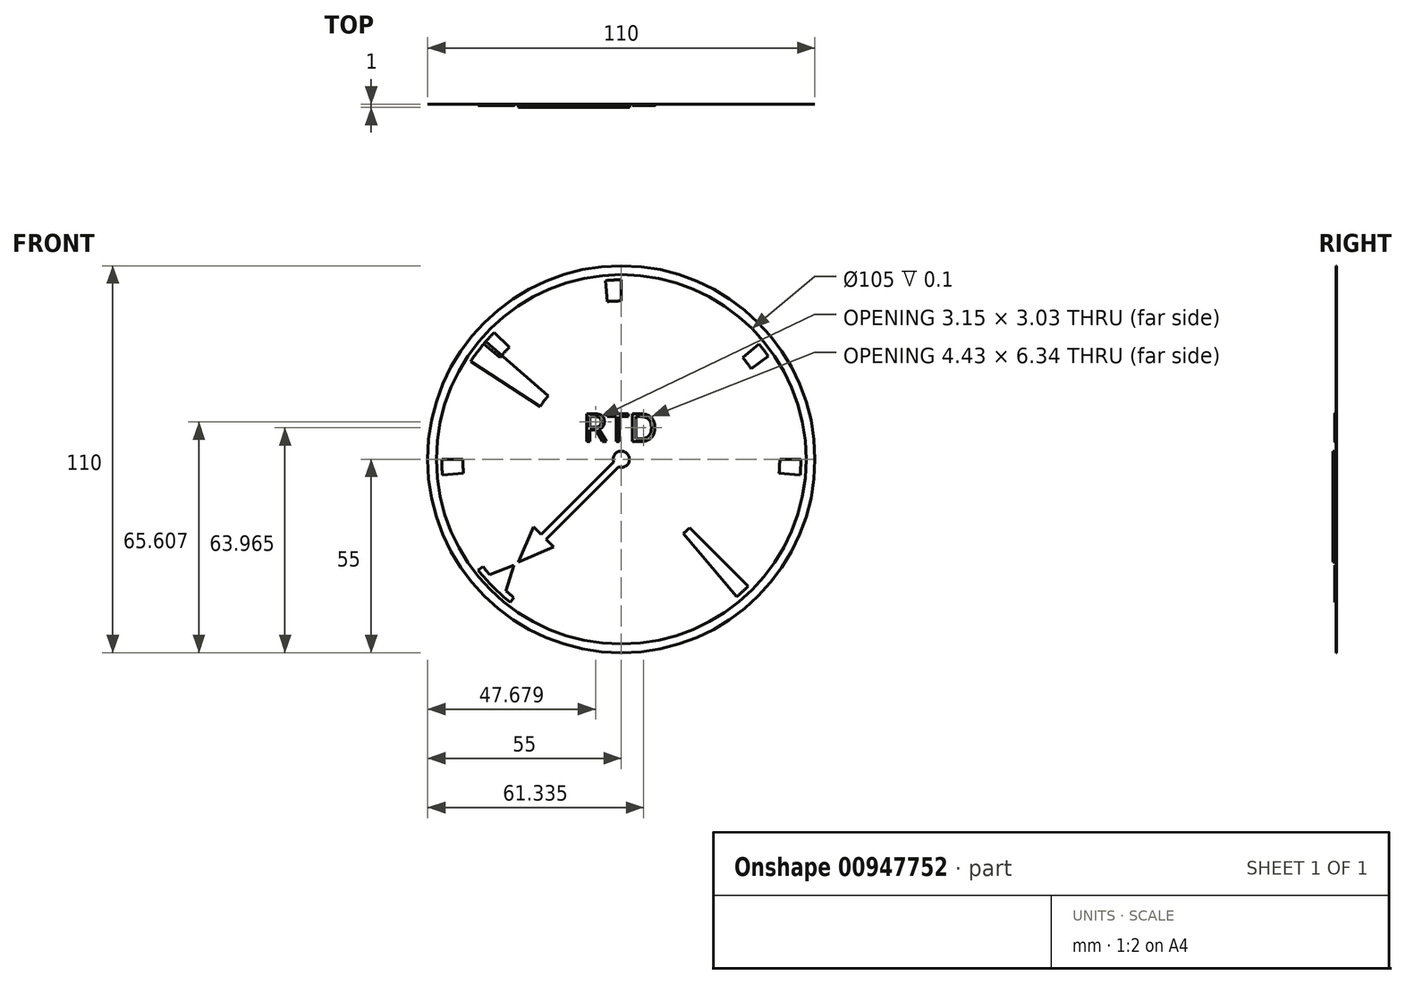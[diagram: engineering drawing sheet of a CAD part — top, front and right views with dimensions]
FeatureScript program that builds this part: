
annotation { "Feature Type Name" : "Feature", "Feature Type Description" : "" }
export const myFeature = defineFeature(function(context is Context, id is Id, definition is map)
    precondition{}
    {
        {
            var Q0;
            Q0=qCreatedBy(makeId("Right.planeOp"),FACE);
            var sketch = newSketch(context, id + "F0", { "sketchPlane" : qUnion([Q0])});
            skLineSegment(sketch, "E0", {"start": v(0, 0) * mm, "end": v(-116.06, 0) * mm, "construction": true});
            skSolve(sketch);
        }
        {
            var Q0;
            Q0=qCreatedBy(makeId("Right.planeOp"),FACE);
            var Q1;
            Q1=sQuery(id+"F0.wireOp",EDGE,"E0");
            cPlane(context, id + "F1", {"entities" : qUnion([Q0, Q1]), "cplaneType" : CPlaneType.LINE_ANGLE, "offset" : 25 * mm, "angle" : 135 * degree, "width" : 150 * mm, "height" : 150 * mm});
        }
        {
            var Q0;
            Q0=qCreatedBy(id+"F1.planeOp",FACE);
            var sketch = newSketch(context, id + "F2", { "sketchPlane" : qUnion([Q0])});
            skLineSegment(sketch, "E1.bottom", {"start": v(-25.4, 0) * mm, "end": v(-50.8, 0) * mm});
            skLineSegment(sketch, "E1.top", {"start": v(-25.4, 0) * mm, "end": v(-50.8, 0) * mm});
            skLineSegment(sketch, "E1.left", {"start": v(-25.4, 0) * mm, "end": v(-25.4, 0) * mm});
            skLineSegment(sketch, "E1.right", {"start": v(-50.8, 0) * mm, "end": v(-50.8, 0) * mm});
            skSolve(sketch);
        }
        {
            var Q0;
            Q0=qSketchRegion(id+"F2",true);
            var Q1;
            Q1=sQuery(id+"F0.wireOp",EDGE,"E0");
            revolve(context, id + "F3", {"surfaceOperationType" : NewSurfaceOperationType.NEW, "entities" : qUnion([Q0]), "axis" : qUnion([Q1]), "revolveType" : RevolveType.ONE_DIRECTION, "oppositeDirection" : true, "angle" : 135 * degree});
        }
        {
            var Q0;
            Q0=qCreatedBy(makeId("Right.planeOp"),FACE);
            var sketch = newSketch(context, id + "F4", { "sketchPlane" : qUnion([Q0])});
            skLineSegment(sketch, "E2.bottom", {"start": v(-0.01, 50.8) * mm, "end": v(0, 50.8) * mm});
            skLineSegment(sketch, "E2.top", {"start": v(0, 25.4) * mm, "end": v(0, 25.4) * mm});
            skLineSegment(sketch, "E2.left", {"start": v(-0.01, 50.8) * mm, "end": v(0, 25.4) * mm});
            skLineSegment(sketch, "E2.right", {"start": v(0, 50.8) * mm, "end": v(0, 25.4) * mm});
            skSolve(sketch);
        }
        {
            var Q0;
            Q0=qSketchRegion(id+"F4",true);
            var Q1;
            Q1=sQuery(id+"F0.wireOp",EDGE,"E0");
            revolve(context, id + "F5", {"surfaceOperationType" : NewSurfaceOperationType.NEW, "entities" : qUnion([Q0]), "axis" : qUnion([Q1]), "revolveType" : RevolveType.ONE_DIRECTION, "oppositeDirection" : true, "angle" : 2 * degree});
        }
        {
            var Q0;
            Q0=qCreatedBy(makeId("Right.planeOp"),FACE);
            var Q1;
            Q1=sQuery(id+"F0.wireOp",EDGE,"E0");
            cPlane(context, id + "F6", {"entities" : qUnion([Q0, Q1]), "cplaneType" : CPlaneType.LINE_ANGLE, "offset" : 25 * mm, "angle" : 2 * degree, "oppositeDirection" : true, "width" : 150 * mm, "height" : 150 * mm});
        }
        {
            var Q0;
            Q0=qCreatedBy(id+"F6.planeOp",FACE);
            var sketch = newSketch(context, id + "F7", { "sketchPlane" : qUnion([Q0])});
            skLineSegment(sketch, "E3.bottom", {"start": v(0, 50.8) * mm, "end": v(0, 50.8) * mm});
            skLineSegment(sketch, "E3.top", {"start": v(0, 25.4) * mm, "end": v(0, 25.4) * mm});
            skLineSegment(sketch, "E3.left", {"start": v(0, 50.8) * mm, "end": v(0, 25.4) * mm});
            skLineSegment(sketch, "E3.right", {"start": v(0, 50.8) * mm, "end": v(0, 25.4) * mm});
            skSolve(sketch);
        }
        {
            var Q0;
            Q0=qSketchRegion(id+"F7",true);
            var Q1;
            Q1=sQuery(id+"F0.wireOp",EDGE,"E0");
            revolve(context, id + "F8", {"surfaceOperationType" : NewSurfaceOperationType.NEW, "entities" : qUnion([Q0]), "axis" : qUnion([Q1]), "revolveType" : RevolveType.ONE_DIRECTION, "oppositeDirection" : true, "angle" : 60 * degree});
        }
        {
            var Q0;
            Q0=qCreatedBy(id+"F6.planeOp",FACE);
            var Q1;
            Q1=sQuery(id+"F0.wireOp",EDGE,"E0");
            cPlane(context, id + "F9", {"entities" : qUnion([Q0, Q1]), "cplaneType" : CPlaneType.LINE_ANGLE, "offset" : 25 * mm, "angle" : 60 * degree, "oppositeDirection" : true, "width" : 150 * mm, "height" : 150 * mm});
        }
        {
            var Q0;
            Q0=qCreatedBy(id+"F9.planeOp",FACE);
            var sketch = newSketch(context, id + "F10", { "sketchPlane" : qUnion([Q0])});
            skLineSegment(sketch, "E4.bottom", {"start": v(50.8, 0) * mm, "end": v(25.4, 0) * mm});
            skLineSegment(sketch, "E4.top", {"start": v(50.8, 0) * mm, "end": v(25.4, -0.01) * mm});
            skLineSegment(sketch, "E4.left", {"start": v(50.8, 0) * mm, "end": v(50.8, 0) * mm});
            skLineSegment(sketch, "E4.right", {"start": v(25.4, 0) * mm, "end": v(25.4, -0.01) * mm});
            skSolve(sketch);
        }
        {
            var Q0;
            Q0=qSketchRegion(id+"F10",true);
            var Q1;
            Q1=sQuery(id+"F0.wireOp",EDGE,"E0");
            revolve(context, id + "F11", {"surfaceOperationType" : NewSurfaceOperationType.NEW, "entities" : qUnion([Q0]), "axis" : qUnion([Q1]), "revolveType" : RevolveType.ONE_DIRECTION, "oppositeDirection" : true, "angle" : 2 * degree});
        }
        {
            var Q0;
            Q0=qCreatedBy(makeId("Front.planeOp"),FACE);
            var sketch = newSketch(context, id + "F12", { "sketchPlane" : qUnion([Q0])});
            skLineSegment(sketch, "E5.bottom", {"start": v(-0.77, -2.19) * mm, "end": v(-24.04, -25.46) * mm});
            skLineSegment(sketch, "E5.top", {"start": v(-2.19, -0.77) * mm, "end": v(-25.46, -24.04) * mm});
            skPoint(sketch, "E5.middle", {"position": v(0, 0) * mm});
            skLineSegment(sketch, "E6", {"start": v(0, 0) * mm, "end": v(0, 10.99) * mm, "construction": true});
            skPoint(sketch, "E7", {"position": v(-24.75, -24.75) * mm});
            skCircle(sketch, "E8", {"center": v(-24.75, -24.75) * mm, "radius": 10.19 * mm, "construction": true});
            skLineSegment(sketch, "E9", {"start": v(-24.04, -25.46) * mm, "end": v(-21.92, -27.58) * mm});
            skLineSegment(sketch, "E10", {"start": v(-25.46, -24.04) * mm, "end": v(-27.58, -21.92) * mm});
            skLineSegment(sketch, "E11", {"start": v(-24.75, -24.75) * mm, "end": v(-31.95, -31.95) * mm, "construction": true});
            skLineSegment(sketch, "E12", {"start": v(-31.95, -31.95) * mm, "end": v(-27.58, -21.92) * mm});
            skLineSegment(sketch, "E13", {"start": v(-21.92, -27.58) * mm, "end": v(-31.95, -31.95) * mm});
            skArc(sketch, "E14", {"start": v(-0.77, -2.19) * mm, "mid": v(1.64, 1.64) * mm, "end": v(-2.19, -0.77) * mm});
            skPoint(sketch, "E15.orphan", {"position": v(-0.7, 0.7) * mm});
            skPoint(sketch, "E16.end.orphan", {"position": v(0.7, -0.7) * mm});
            skSolve(sketch);
        }
        {
            var Q0;
            Q0=qSketchRegion(id+"F12",true);
            extrude(context, id + "F13", {"entities" : qUnion([Q0]), "depth" : 1 * mm, "offsetDistance" : 25 * mm});
        }
        {
            var Q0;
            Q0=qCreatedBy(makeId("Front.planeOp"),FACE);
            var sketch = newSketch(context, id + "F14", { "sketchPlane" : qUnion([Q0])});
            skCircle(sketch, "E17", {"center": v(0, 0) * mm, "radius": 52.5 * mm});
            skCircle(sketch, "E18", {"center": v(0, 0) * mm, "radius": 55 * mm});
            skSolve(sketch);
        }
        {
            var Q0;
            Q0=qSketchRegion(id+"F14",true);
            extrude(context, id + "F15", {"entities" : qUnion([Q0]), "depth" : .1 * mm, "offsetDistance" : 25 * mm});
        }
        {
            var Q0;
            Q0=qCreatedBy(makeId("Front.planeOp"),FACE);
            var sketch = newSketch(context, id + "F16", { "sketchPlane" : qUnion([Q0])});
            skCircle(sketch, "E19", {"center": v(130, 0) * mm, "radius": 52.5 * mm});
            skCircle(sketch, "E20", {"center": v(130, 0) * mm, "radius": 55 * mm});
            skSolve(sketch);
        }
        {
            var Q0;
            Q0=qSketchRegion(id+"F16",true);
            extrude(context, id + "F17", {"entities" : qUnion([Q0]), "depth" : .1 * mm, "offsetDistance" : 25 * mm});
        }
        {
            var Q0;
            Q0=qCreatedBy(makeId("Front.planeOp"),FACE);
            var sketch = newSketch(context, id + "F18", { "sketchPlane" : qUnion([Q0])});
            skArc(sketch, "E21", {"start": v(79.2, -4.44) * mm, "mid": v(79.05, -2.22) * mm, "end": v(79, 0) * mm});
            skLineSegment(sketch, "E22", {"start": v(79, 0) * mm, "end": v(85, 0) * mm});
            skLineSegment(sketch, "E23", {"start": v(85.17, -3.92) * mm, "end": v(79.2, -4.44) * mm});
            skArc(sketch, "E24", {"start": v(85, 0) * mm, "mid": v(85.04, -1.96) * mm, "end": v(85.17, -3.92) * mm});
            skSolve(sketch);
        }
        {
            var Q0;
            Q0=qSketchRegion(id+"F18",true);
            extrude(context, id + "F19", {"entities" : qUnion([Q0]), "depth" : .1 * mm, "offsetDistance" : 25 * mm});
        }
        {
            var Q0;
            Q0=qCreatedBy(makeId("Front.planeOp"),FACE);
            var sketch = newSketch(context, id + "F20", { "sketchPlane" : qUnion([Q0])});
            skLineSegment(sketch, "E25", {"start": v(130, 0) * mm, "end": v(223.12, 0) * mm, "construction": true});
            skLineSegment(sketch, "E26", {"start": v(147.68, -21.07) * mm, "end": v(162.78, -39.07) * mm});
            skArc(sketch, "E27", {"start": v(147.68, -21.07) * mm, "mid": v(148.58, -20.28) * mm, "end": v(149.45, -19.45) * mm});
            skArc(sketch, "E28", {"start": v(162.78, -39.07) * mm, "mid": v(164.46, -37.6) * mm, "end": v(166.06, -36.06) * mm});
            skLineSegment(sketch, "E29", {"start": v(149.45, -19.45) * mm, "end": v(166.06, -36.06) * mm});
            skSolve(sketch);
        }
        {
            var Q0;
            Q0=qSketchRegion(id+"F20",true);
            extrude(context, id + "F21", {"entities" : qUnion([Q0]), "depth" : .1 * mm, "offsetDistance" : 25 * mm});
        }
        {
            var Q0;
            Q0=qCreatedBy(makeId("Front.planeOp"),FACE);
            var sketch = newSketch(context, id + "F22", { "sketchPlane" : qUnion([Q0])});
            skLineSegment(sketch, "E30", {"start": v(130, 45) * mm, "end": v(130, 51) * mm});
            skLineSegment(sketch, "E31", {"start": v(126.08, 44.83) * mm, "end": v(125.56, 50.8) * mm});
            skArc(sketch, "E32", {"start": v(126.08, 44.83) * mm, "mid": v(128.04, 44.96) * mm, "end": v(130, 45) * mm});
            skArc(sketch, "E33", {"start": v(125.56, 50.8) * mm, "mid": v(127.78, 50.95) * mm, "end": v(130, 51) * mm});
            skSolve(sketch);
        }
        {
            var Q0;
            Q0=qSketchRegion(id+"F22",true);
            extrude(context, id + "F23", {"entities" : qUnion([Q0]), "depth" : .1 * mm, "offsetDistance" : 25 * mm});
        }
        {
            var Q0;
            Q0=qCreatedBy(makeId("Front.planeOp"),FACE);
            var sketch = newSketch(context, id + "F24", { "sketchPlane" : qUnion([Q0])});
            skLineSegment(sketch, "E34", {"start": v(98.18, 31.82) * mm, "end": v(93.94, 36.06) * mm});
            skLineSegment(sketch, "E35", {"start": v(130, 0) * mm, "end": v(130, 16.9) * mm, "construction": true});
            skLineSegment(sketch, "E36", {"start": v(95.53, 28.93) * mm, "end": v(90.93, 32.78) * mm});
            skArc(sketch, "E37", {"start": v(93.94, 36.06) * mm, "mid": v(92.4, 34.46) * mm, "end": v(90.93, 32.78) * mm});
            skArc(sketch, "E38", {"start": v(98.18, 31.82) * mm, "mid": v(96.82, 30.4) * mm, "end": v(95.53, 28.93) * mm});
            skSolve(sketch);
        }
        {
            var Q0;
            Q0=qSketchRegion(id+"F24",true);
            extrude(context, id + "F25", {"entities" : qUnion([Q0]), "depth" : .1 * mm, "offsetDistance" : 25 * mm});
        }
        {
            var Q0;
            Q0=qCreatedBy(makeId("Front.planeOp"),FACE);
            var sketch = newSketch(context, id + "F26", { "sketchPlane" : qUnion([Q0])});
            skLineSegment(sketch, "E39", {"start": v(164.47, 28.93) * mm, "end": v(169.07, 32.78) * mm});
            skLineSegment(sketch, "E40", {"start": v(130, 0) * mm, "end": v(130, 13.97) * mm, "construction": true});
            skLineSegment(sketch, "E41", {"start": v(166.86, 25.81) * mm, "end": v(171.78, 29.25) * mm});
            skArc(sketch, "E42", {"start": v(164.47, 28.93) * mm, "mid": v(165.7, 27.4) * mm, "end": v(166.86, 25.81) * mm});
            skArc(sketch, "E43", {"start": v(169.07, 32.78) * mm, "mid": v(170.46, 31.05) * mm, "end": v(171.78, 29.25) * mm});
            skSolve(sketch);
        }
        {
            var Q0;
            Q0=qSketchRegion(id+"F26",true);
            extrude(context, id + "F27", {"entities" : qUnion([Q0]), "depth" : .1 * mm, "offsetDistance" : 25 * mm});
        }
        {
            var Q0;
            Q0=qCreatedBy(makeId("Front.planeOp"),FACE);
            var sketch = newSketch(context, id + "F28", { "sketchPlane" : qUnion([Q0])});
            skLineSegment(sketch, "E44", {"start": v(175, 0) * mm, "end": v(181, 0) * mm});
            skLineSegment(sketch, "E45", {"start": v(174.83, -3.92) * mm, "end": v(180.8, -4.44) * mm});
            skArc(sketch, "E46", {"start": v(181, 0) * mm, "mid": v(180.95, -2.22) * mm, "end": v(180.8, -4.44) * mm});
            skArc(sketch, "E47", {"start": v(175, 0) * mm, "mid": v(174.96, -1.96) * mm, "end": v(174.83, -3.92) * mm});
            skSolve(sketch);
        }
        {
            var Q0;
            Q0=qSketchRegion(id+"F28",true);
            extrude(context, id + "F29", {"entities" : qUnion([Q0]), "depth" : .1 * mm, "offsetDistance" : 25 * mm});
        }
        {
            var Q0;
            Q0=qCreatedBy(makeId("Front.planeOp"),FACE);
            var sketch = newSketch(context, id + "F30", { "sketchPlane" : qUnion([Q0])});
            skLineSegment(sketch, "E48.bottom", {"start": v(129.23, -2.19) * mm, "end": v(108.62, -22.8) * mm});
            skLineSegment(sketch, "E48.top", {"start": v(127.81, -0.77) * mm, "end": v(107.2, -21.38) * mm});
            skPoint(sketch, "E48.middle", {"position": v(130, 0) * mm});
            skLineSegment(sketch, "E49", {"start": v(130, 0) * mm, "end": v(130, 10.99) * mm, "construction": true});
            skPoint(sketch, "E50", {"position": v(107.9, -22.1) * mm});
            skCircle(sketch, "E51", {"center": v(107.9, -22.1) * mm, "radius": 10.19 * mm, "construction": true});
            skLineSegment(sketch, "E52", {"start": v(108.62, -22.8) * mm, "end": v(110.74, -24.92) * mm});
            skLineSegment(sketch, "E53", {"start": v(107.2, -21.38) * mm, "end": v(105.08, -19.26) * mm});
            skLineSegment(sketch, "E54", {"start": v(107.9, -22.1) * mm, "end": v(100.7, -29.3) * mm, "construction": true});
            skLineSegment(sketch, "E55", {"start": v(100.7, -29.3) * mm, "end": v(105.08, -19.26) * mm});
            skLineSegment(sketch, "E56", {"start": v(110.74, -24.92) * mm, "end": v(100.7, -29.3) * mm});
            skArc(sketch, "E57", {"start": v(129.23, -2.19) * mm, "mid": v(131.64, 1.64) * mm, "end": v(127.81, -0.77) * mm});
            skPoint(sketch, "E58.orphan", {"position": v(129.3, 0.7) * mm});
            skPoint(sketch, "E59.end.orphan", {"position": v(130.7, -0.7) * mm});
            skSolve(sketch);
        }
        {
            var Q0;
            Q0=qSketchRegion(id+"F30",true);
            extrude(context, id + "F31", {"entities" : qUnion([Q0]), "depth" : 1 * mm, "offsetDistance" : 25 * mm});
        }
        {
            var Q0;
            Q0=qCreatedBy(makeId("Front.planeOp"),FACE);
            var sketch = newSketch(context, id + "F32", { "sketchPlane" : qUnion([Q0])});
            skLineSegment(sketch, "E60", {"start": v(0, 0) * mm, "end": v(130, 0) * mm, "construction": true});
            skLineSegment(sketch, "E61.bottom", {"start": v(194.42, -63.85) * mm, "end": v(-64.42, -63.85) * mm});
            skLineSegment(sketch, "E61.top", {"start": v(194.42, 63.85) * mm, "end": v(-64.42, 63.85) * mm});
            skLineSegment(sketch, "E61.left", {"start": v(194.42, -63.85) * mm, "end": v(194.42, 63.85) * mm});
            skLineSegment(sketch, "E61.right", {"start": v(-64.42, -63.85) * mm, "end": v(-64.42, 63.85) * mm});
            skPoint(sketch, "E61.middle", {"position": v(65, 0) * mm});
            skLineSegment(sketch, "E62.bottom", {"start": v(198.42, -67.85) * mm, "end": v(-68.42, -67.85) * mm});
            skLineSegment(sketch, "E62.top", {"start": v(198.42, 67.85) * mm, "end": v(-68.42, 67.85) * mm});
            skLineSegment(sketch, "E62.left", {"start": v(198.42, -67.85) * mm, "end": v(198.42, 67.85) * mm});
            skLineSegment(sketch, "E62.right", {"start": v(-68.42, -67.85) * mm, "end": v(-68.42, 67.85) * mm});
            skText(sketch, "E63", { "text": "SPEED", "fontName": "OpenSans-Bold.ttf"});
            skText(sketch, "E64", { "text": "TENSION", "fontName": "OpenSans-Regular.ttf"});
            skLineSegment(sketch, "E65", {"start": v(-15.3, -30.02) * mm, "end": v(165.4, -30.02) * mm, "construction": true});
            const initialGuessF32  = {"E63": [-0.0153, -0.03702, 1, 0, 0.007], "E64": [0.10955, -0.03702, 1, 0, 0.007]};
            skSetInitialGuess(sketch, initialGuessF32);
            skSolve(sketch);
        }
        {
            var Q0;
            Q0=qSketchRegion(id+"F32",true);
            extrude(context, id + "F33", {"entities" : qUnion([Q0]), "depth" : .1 * mm, "offsetDistance" : 25 * mm});
        }
        {
            var Q0;
            Q0=qCreatedBy(makeId("Front.planeOp"),FACE);
            var sketch = newSketch(context, id + "F34", { "sketchPlane" : qUnion([Q0])});
            skLineSegment(sketch, "E66", {"start": v(3.26, -76.77) * mm, "end": v(133.26, -76.77) * mm, "construction": true});
            skPoint(sketch, "E67.middle", {"position": v(68.26, -76.77) * mm});
            skText(sketch, "E68", { "text": "SPEED", "fontName": "OpenSans-Bold.ttf"});
            skText(sketch, "E69", { "text": "TENSION", "fontName": "OpenSans-Bold.ttf"});
            skLineSegment(sketch, "E70", {"start": v(-15, -30.02) * mm, "end": v(168.67, -30.02) * mm, "construction": true});
            skPoint(sketch, "E71", {"position": v(76.84, -30.02) * mm});
            skLineSegment(sketch, "E72", {"start": v(0, 0) * mm, "end": v(0, -24.7) * mm, "construction": true});
            const initialGuessF34  = {"E68": [-0.015, -0.03702, 1, 0, 0.007], "E69": [0.109, -0.03702, 1, 0, 0.007]};
            skSetInitialGuess(sketch, initialGuessF34);
            skSolve(sketch);
        }
        {
            var Q0;
            Q0=qSketchRegion(id+"F34",true);
            extrude(context, id + "F35", {"entities" : qUnion([Q0]), "depth" : .1 * mm, "offsetDistance" : 25 * mm});
        }
        {
            var Q0;
            Q0=makeQuery(id+"F35.opExtrude","SWEPT_BODY",BODY,{"disambiguationData":[OSD([sQuery(id+"F34.wireOp",EDGE,"E68.sketch_text.stroke-56"),sQuery(id+"F34.wireOp",EDGE,"E68.sketch_text.stroke-57"),sQuery(id+"F34.wireOp",EDGE,"E68.sketch_text.stroke-58"),sQuery(id+"F34.wireOp",EDGE,"E68.sketch_text.stroke-59"),sQuery(id+"F34.wireOp",EDGE,"E68.sketch_text.stroke-60"),sQuery(id+"F34.wireOp",EDGE,"E68.sketch_text.stroke-61"),sQuery(id+"F34.wireOp",EDGE,"E68.sketch_text.stroke-62"),sQuery(id+"F34.wireOp",EDGE,"E68.sketch_text.stroke-63"),sQuery(id+"F34.wireOp",EDGE,"E68.sketch_text.stroke-64"),sQuery(id+"F34.wireOp",EDGE,"E68.sketch_text.stroke-65"),sQuery(id+"F34.wireOp",EDGE,"E68.sketch_text.stroke-66"),sQuery(id+"F34.wireOp",EDGE,"E68.sketch_text.stroke-67")])]});
            var Q1;
            Q1=makeQuery(id+"F35.opExtrude","SWEPT_BODY",BODY,{"disambiguationData":[OSD([sQuery(id+"F34.wireOp",EDGE,"E68.sketch_text.stroke-44"),sQuery(id+"F34.wireOp",EDGE,"E68.sketch_text.stroke-45"),sQuery(id+"F34.wireOp",EDGE,"E68.sketch_text.stroke-46"),sQuery(id+"F34.wireOp",EDGE,"E68.sketch_text.stroke-47"),sQuery(id+"F34.wireOp",EDGE,"E68.sketch_text.stroke-48"),sQuery(id+"F34.wireOp",EDGE,"E68.sketch_text.stroke-49"),sQuery(id+"F34.wireOp",EDGE,"E68.sketch_text.stroke-50"),sQuery(id+"F34.wireOp",EDGE,"E68.sketch_text.stroke-51"),sQuery(id+"F34.wireOp",EDGE,"E68.sketch_text.stroke-52"),sQuery(id+"F34.wireOp",EDGE,"E68.sketch_text.stroke-53"),sQuery(id+"F34.wireOp",EDGE,"E68.sketch_text.stroke-54"),sQuery(id+"F34.wireOp",EDGE,"E68.sketch_text.stroke-55")])]});
            var Q2;
            Q2=makeQuery(id+"F35.opExtrude","SWEPT_BODY",BODY,{"disambiguationData":[OSD([sQuery(id+"F34.wireOp",EDGE,"E68.sketch_text.stroke-68"),sQuery(id+"F34.wireOp",EDGE,"E68.sketch_text.stroke-69"),sQuery(id+"F34.wireOp",EDGE,"E68.sketch_text.stroke-70"),sQuery(id+"F34.wireOp",EDGE,"E68.sketch_text.stroke-71"),sQuery(id+"F34.wireOp",EDGE,"E68.sketch_text.stroke-72"),sQuery(id+"F34.wireOp",EDGE,"E68.sketch_text.stroke-73"),sQuery(id+"F34.wireOp",EDGE,"E68.sketch_text.stroke-74"),sQuery(id+"F34.wireOp",EDGE,"E68.sketch_text.stroke-75"),sQuery(id+"F34.wireOp",EDGE,"E68.sketch_text.stroke-76"),sQuery(id+"F34.wireOp",EDGE,"E68.sketch_text.stroke-77"),sQuery(id+"F34.wireOp",EDGE,"E68.sketch_text.stroke-78"),sQuery(id+"F34.wireOp",EDGE,"E68.sketch_text.stroke-79")])]});
            var Q3;
            Q3=makeQuery(id+"F35.opExtrude","SWEPT_BODY",BODY,{"disambiguationData":[OSD([sQuery(id+"F34.wireOp",EDGE,"E68.sketch_text.stroke-28"),sQuery(id+"F34.wireOp",EDGE,"E68.sketch_text.stroke-29"),sQuery(id+"F34.wireOp",EDGE,"E68.sketch_text.stroke-30"),sQuery(id+"F34.wireOp",EDGE,"E68.sketch_text.stroke-31"),sQuery(id+"F34.wireOp",EDGE,"E68.sketch_text.stroke-32"),sQuery(id+"F34.wireOp",EDGE,"E68.sketch_text.stroke-33"),sQuery(id+"F34.wireOp",EDGE,"E68.sketch_text.stroke-34"),sQuery(id+"F34.wireOp",EDGE,"E68.sketch_text.stroke-35"),sQuery(id+"F34.wireOp",EDGE,"E68.sketch_text.stroke-36"),sQuery(id+"F34.wireOp",EDGE,"E68.sketch_text.stroke-37"),sQuery(id+"F34.wireOp",EDGE,"E68.sketch_text.stroke-38"),sQuery(id+"F34.wireOp",EDGE,"E68.sketch_text.stroke-39"),sQuery(id+"F34.wireOp",EDGE,"E68.sketch_text.stroke-40"),sQuery(id+"F34.wireOp",EDGE,"E68.sketch_text.stroke-41"),sQuery(id+"F34.wireOp",EDGE,"E68.sketch_text.stroke-42"),sQuery(id+"F34.wireOp",EDGE,"E68.sketch_text.stroke-43")])]});
            var Q4;
            Q4=makeQuery(id+"F35.opExtrude","SWEPT_BODY",BODY,{"disambiguationData":[OSD([sQuery(id+"F34.wireOp",EDGE,"E68.sketch_text.stroke-0"),sQuery(id+"F34.wireOp",EDGE,"E68.sketch_text.stroke-1"),sQuery(id+"F34.wireOp",EDGE,"E68.sketch_text.stroke-2"),sQuery(id+"F34.wireOp",EDGE,"E68.sketch_text.stroke-3"),sQuery(id+"F34.wireOp",EDGE,"E68.sketch_text.stroke-4"),sQuery(id+"F34.wireOp",EDGE,"E68.sketch_text.stroke-5"),sQuery(id+"F34.wireOp",EDGE,"E68.sketch_text.stroke-6"),sQuery(id+"F34.wireOp",EDGE,"E68.sketch_text.stroke-7"),sQuery(id+"F34.wireOp",EDGE,"E68.sketch_text.stroke-8"),sQuery(id+"F34.wireOp",EDGE,"E68.sketch_text.stroke-9"),sQuery(id+"F34.wireOp",EDGE,"E68.sketch_text.stroke-10"),sQuery(id+"F34.wireOp",EDGE,"E68.sketch_text.stroke-11"),sQuery(id+"F34.wireOp",EDGE,"E68.sketch_text.stroke-12"),sQuery(id+"F34.wireOp",EDGE,"E68.sketch_text.stroke-13"),sQuery(id+"F34.wireOp",EDGE,"E68.sketch_text.stroke-14"),sQuery(id+"F34.wireOp",EDGE,"E68.sketch_text.stroke-15"),sQuery(id+"F34.wireOp",EDGE,"E68.sketch_text.stroke-16"),sQuery(id+"F34.wireOp",EDGE,"E68.sketch_text.stroke-17"),sQuery(id+"F34.wireOp",EDGE,"E68.sketch_text.stroke-18"),sQuery(id+"F34.wireOp",EDGE,"E68.sketch_text.stroke-19"),sQuery(id+"F34.wireOp",EDGE,"E68.sketch_text.stroke-20"),sQuery(id+"F34.wireOp",EDGE,"E68.sketch_text.stroke-21"),sQuery(id+"F34.wireOp",EDGE,"E68.sketch_text.stroke-22"),sQuery(id+"F34.wireOp",EDGE,"E68.sketch_text.stroke-23"),sQuery(id+"F34.wireOp",EDGE,"E68.sketch_text.stroke-24"),sQuery(id+"F34.wireOp",EDGE,"E68.sketch_text.stroke-25"),sQuery(id+"F34.wireOp",EDGE,"E68.sketch_text.stroke-26"),sQuery(id+"F34.wireOp",EDGE,"E68.sketch_text.stroke-27")])]});
            var Q5;
            Q5=makeQuery(id+"F15.opExtrude","SWEPT_BODY",BODY,{"disambiguationData":[OSD([sQuery(id+"F14.wireOp",EDGE,"E17"),sQuery(id+"F14.wireOp",EDGE,"E18")])]});
            var Q6;
            Q6=makeQuery(id+"F13.opExtrude","SWEPT_BODY",BODY,{"disambiguationData":[OSD([sQuery(id+"F12.wireOp",EDGE,"E5.bottom"),sQuery(id+"F12.wireOp",EDGE,"E5.top"),sQuery(id+"F12.wireOp",EDGE,"E9"),sQuery(id+"F12.wireOp",EDGE,"E10"),sQuery(id+"F12.wireOp",EDGE,"E12"),sQuery(id+"F12.wireOp",EDGE,"E13"),sQuery(id+"F12.wireOp",EDGE,"E14")])]});
            var Q7;
            Q7=makeQuery(id+"F11.opRevolve","SWEPT_BODY",BODY,{"disambiguationData":[OSD([sQuery(id+"F10.wireOp",EDGE,"E4.bottom"),sQuery(id+"F10.wireOp",EDGE,"E4.top"),sQuery(id+"F10.wireOp",EDGE,"E4.left"),sQuery(id+"F10.wireOp",EDGE,"E4.right")])]});
            var Q8;
            Q8=makeQuery(id+"F8.opRevolve","SWEPT_BODY",BODY,{"disambiguationData":[OSD([sQuery(id+"F7.wireOp",EDGE,"E3.bottom"),sQuery(id+"F7.wireOp",EDGE,"E3.top"),sQuery(id+"F7.wireOp",EDGE,"E3.left"),sQuery(id+"F7.wireOp",EDGE,"E3.right")])]});
            var Q9;
            Q9=makeQuery(id+"F5.opRevolve","SWEPT_BODY",BODY,{"disambiguationData":[OSD([sQuery(id+"F4.wireOp",EDGE,"E2.bottom"),sQuery(id+"F4.wireOp",EDGE,"E2.top"),sQuery(id+"F4.wireOp",EDGE,"E2.left"),sQuery(id+"F4.wireOp",EDGE,"E2.right")])]});
            var Q10;
            Q10=makeQuery(id+"F3.opRevolve","SWEPT_BODY",BODY,{"disambiguationData":[OSD([sQuery(id+"F2.wireOp",EDGE,"E1.bottom"),sQuery(id+"F2.wireOp",EDGE,"E1.top"),sQuery(id+"F2.wireOp",EDGE,"E1.left"),sQuery(id+"F2.wireOp",EDGE,"E1.right")])]});
            deleteBodies(context, id + "F36", {"entities" : qUnion([Q0, Q1, Q2, Q3, Q4, Q5, Q6, Q7, Q8, Q9, Q10])});
        }
        {
            var Q0;
            Q0=makeQuery(id+"F33.opExtrude","SWEPT_BODY",BODY,{"disambiguationData":[OSD([sQuery(id+"F32.wireOp",EDGE,"E61.bottom"),sQuery(id+"F32.wireOp",EDGE,"E61.top"),sQuery(id+"F32.wireOp",EDGE,"E61.left"),sQuery(id+"F32.wireOp",EDGE,"E61.right"),sQuery(id+"F32.wireOp",EDGE,"E62.bottom"),sQuery(id+"F32.wireOp",EDGE,"E62.top"),sQuery(id+"F32.wireOp",EDGE,"E62.left"),sQuery(id+"F32.wireOp",EDGE,"E62.right")])]});
            deleteBodies(context, id + "F37", {"entities" : qUnion([Q0])});
        }
        {
            var Q0;
            Q0=qCreatedBy(makeId("Front.planeOp"),FACE);
            var sketch = newSketch(context, id + "F38", { "sketchPlane" : qUnion([Q0])});
            skLineSegment(sketch, "E73", {"start": v(109.25, 18.04) * mm, "end": v(91.5, 33.46) * mm});
            skLineSegment(sketch, "E74", {"start": v(106.94, 14.98) * mm, "end": v(87.23, 27.78) * mm});
            skArc(sketch, "E75", {"start": v(91.5, 33.46) * mm, "mid": v(89.27, 30.7) * mm, "end": v(87.23, 27.78) * mm});
            skArc(sketch, "E76", {"start": v(109.25, 18.04) * mm, "mid": v(108.04, 16.55) * mm, "end": v(106.94, 14.98) * mm});
            skSolve(sketch);
        }
        {
            var Q0;
            Q0 = qSketchRegion(id + "F38", true);
            extrude(context, id + "F39", {"entities" : qUnion([Q0]), "depth" : .1 * mm, "offsetDistance" : 25 * mm});
        }
        {
            var Q0;
            Q0=makeQuery(id+"F35.opExtrude","SWEPT_BODY",BODY,{"disambiguationData":[OSD([sQuery(id+"F34.wireOp",EDGE,"E69.sketch_text.stroke-80"),sQuery(id+"F34.wireOp",EDGE,"E69.sketch_text.stroke-81"),sQuery(id+"F34.wireOp",EDGE,"E69.sketch_text.stroke-82"),sQuery(id+"F34.wireOp",EDGE,"E69.sketch_text.stroke-83"),sQuery(id+"F34.wireOp",EDGE,"E69.sketch_text.stroke-84"),sQuery(id+"F34.wireOp",EDGE,"E69.sketch_text.stroke-85"),sQuery(id+"F34.wireOp",EDGE,"E69.sketch_text.stroke-86"),sQuery(id+"F34.wireOp",EDGE,"E69.sketch_text.stroke-87"),sQuery(id+"F34.wireOp",EDGE,"E69.sketch_text.stroke-88"),sQuery(id+"F34.wireOp",EDGE,"E69.sketch_text.stroke-89"),sQuery(id+"F34.wireOp",EDGE,"E69.sketch_text.stroke-90"),sQuery(id+"F34.wireOp",EDGE,"E69.sketch_text.stroke-91"),sQuery(id+"F34.wireOp",EDGE,"E69.sketch_text.stroke-92"),sQuery(id+"F34.wireOp",EDGE,"E69.sketch_text.stroke-93")])]});
            var Q1;
            Q1=makeQuery(id+"F35.opExtrude","SWEPT_BODY",BODY,{"disambiguationData":[OSD([sQuery(id+"F34.wireOp",EDGE,"E69.sketch_text.stroke-66"),sQuery(id+"F34.wireOp",EDGE,"E69.sketch_text.stroke-67"),sQuery(id+"F34.wireOp",EDGE,"E69.sketch_text.stroke-68"),sQuery(id+"F34.wireOp",EDGE,"E69.sketch_text.stroke-69"),sQuery(id+"F34.wireOp",EDGE,"E69.sketch_text.stroke-70"),sQuery(id+"F34.wireOp",EDGE,"E69.sketch_text.stroke-71"),sQuery(id+"F34.wireOp",EDGE,"E69.sketch_text.stroke-72"),sQuery(id+"F34.wireOp",EDGE,"E69.sketch_text.stroke-73"),sQuery(id+"F34.wireOp",EDGE,"E69.sketch_text.stroke-74"),sQuery(id+"F34.wireOp",EDGE,"E69.sketch_text.stroke-75"),sQuery(id+"F34.wireOp",EDGE,"E69.sketch_text.stroke-76"),sQuery(id+"F34.wireOp",EDGE,"E69.sketch_text.stroke-77"),sQuery(id+"F34.wireOp",EDGE,"E69.sketch_text.stroke-78"),sQuery(id+"F34.wireOp",EDGE,"E69.sketch_text.stroke-79")])]});
            var Q2;
            Q2=makeQuery(id+"F35.opExtrude","SWEPT_BODY",BODY,{"disambiguationData":[OSD([sQuery(id+"F34.wireOp",EDGE,"E69.sketch_text.stroke-62"),sQuery(id+"F34.wireOp",EDGE,"E69.sketch_text.stroke-63"),sQuery(id+"F34.wireOp",EDGE,"E69.sketch_text.stroke-64"),sQuery(id+"F34.wireOp",EDGE,"E69.sketch_text.stroke-65")])]});
            var Q3;
            Q3=makeQuery(id+"F35.opExtrude","SWEPT_BODY",BODY,{"disambiguationData":[OSD([sQuery(id+"F34.wireOp",EDGE,"E69.sketch_text.stroke-34"),sQuery(id+"F34.wireOp",EDGE,"E69.sketch_text.stroke-35"),sQuery(id+"F34.wireOp",EDGE,"E69.sketch_text.stroke-36"),sQuery(id+"F34.wireOp",EDGE,"E69.sketch_text.stroke-37"),sQuery(id+"F34.wireOp",EDGE,"E69.sketch_text.stroke-38"),sQuery(id+"F34.wireOp",EDGE,"E69.sketch_text.stroke-39"),sQuery(id+"F34.wireOp",EDGE,"E69.sketch_text.stroke-40"),sQuery(id+"F34.wireOp",EDGE,"E69.sketch_text.stroke-41"),sQuery(id+"F34.wireOp",EDGE,"E69.sketch_text.stroke-42"),sQuery(id+"F34.wireOp",EDGE,"E69.sketch_text.stroke-43"),sQuery(id+"F34.wireOp",EDGE,"E69.sketch_text.stroke-44"),sQuery(id+"F34.wireOp",EDGE,"E69.sketch_text.stroke-45"),sQuery(id+"F34.wireOp",EDGE,"E69.sketch_text.stroke-46"),sQuery(id+"F34.wireOp",EDGE,"E69.sketch_text.stroke-47"),sQuery(id+"F34.wireOp",EDGE,"E69.sketch_text.stroke-48"),sQuery(id+"F34.wireOp",EDGE,"E69.sketch_text.stroke-49"),sQuery(id+"F34.wireOp",EDGE,"E69.sketch_text.stroke-50"),sQuery(id+"F34.wireOp",EDGE,"E69.sketch_text.stroke-51"),sQuery(id+"F34.wireOp",EDGE,"E69.sketch_text.stroke-52"),sQuery(id+"F34.wireOp",EDGE,"E69.sketch_text.stroke-53"),sQuery(id+"F34.wireOp",EDGE,"E69.sketch_text.stroke-54"),sQuery(id+"F34.wireOp",EDGE,"E69.sketch_text.stroke-55"),sQuery(id+"F34.wireOp",EDGE,"E69.sketch_text.stroke-56"),sQuery(id+"F34.wireOp",EDGE,"E69.sketch_text.stroke-57"),sQuery(id+"F34.wireOp",EDGE,"E69.sketch_text.stroke-58"),sQuery(id+"F34.wireOp",EDGE,"E69.sketch_text.stroke-59"),sQuery(id+"F34.wireOp",EDGE,"E69.sketch_text.stroke-60"),sQuery(id+"F34.wireOp",EDGE,"E69.sketch_text.stroke-61")])]});
            var Q4;
            Q4=makeQuery(id+"F35.opExtrude","SWEPT_BODY",BODY,{"disambiguationData":[OSD([sQuery(id+"F34.wireOp",EDGE,"E69.sketch_text.stroke-20"),sQuery(id+"F34.wireOp",EDGE,"E69.sketch_text.stroke-21"),sQuery(id+"F34.wireOp",EDGE,"E69.sketch_text.stroke-22"),sQuery(id+"F34.wireOp",EDGE,"E69.sketch_text.stroke-23"),sQuery(id+"F34.wireOp",EDGE,"E69.sketch_text.stroke-24"),sQuery(id+"F34.wireOp",EDGE,"E69.sketch_text.stroke-25"),sQuery(id+"F34.wireOp",EDGE,"E69.sketch_text.stroke-26"),sQuery(id+"F34.wireOp",EDGE,"E69.sketch_text.stroke-27"),sQuery(id+"F34.wireOp",EDGE,"E69.sketch_text.stroke-28"),sQuery(id+"F34.wireOp",EDGE,"E69.sketch_text.stroke-29"),sQuery(id+"F34.wireOp",EDGE,"E69.sketch_text.stroke-30"),sQuery(id+"F34.wireOp",EDGE,"E69.sketch_text.stroke-31"),sQuery(id+"F34.wireOp",EDGE,"E69.sketch_text.stroke-32"),sQuery(id+"F34.wireOp",EDGE,"E69.sketch_text.stroke-33")])]});
            var Q5;
            Q5=makeQuery(id+"F35.opExtrude","SWEPT_BODY",BODY,{"disambiguationData":[OSD([sQuery(id+"F34.wireOp",EDGE,"E69.sketch_text.stroke-8"),sQuery(id+"F34.wireOp",EDGE,"E69.sketch_text.stroke-9"),sQuery(id+"F34.wireOp",EDGE,"E69.sketch_text.stroke-10"),sQuery(id+"F34.wireOp",EDGE,"E69.sketch_text.stroke-11"),sQuery(id+"F34.wireOp",EDGE,"E69.sketch_text.stroke-12"),sQuery(id+"F34.wireOp",EDGE,"E69.sketch_text.stroke-13"),sQuery(id+"F34.wireOp",EDGE,"E69.sketch_text.stroke-14"),sQuery(id+"F34.wireOp",EDGE,"E69.sketch_text.stroke-15"),sQuery(id+"F34.wireOp",EDGE,"E69.sketch_text.stroke-16"),sQuery(id+"F34.wireOp",EDGE,"E69.sketch_text.stroke-17"),sQuery(id+"F34.wireOp",EDGE,"E69.sketch_text.stroke-18"),sQuery(id+"F34.wireOp",EDGE,"E69.sketch_text.stroke-19")])]});
            var Q6;
            Q6=makeQuery(id+"F35.opExtrude","SWEPT_BODY",BODY,{"disambiguationData":[OSD([sQuery(id+"F34.wireOp",EDGE,"E69.sketch_text.stroke-0"),sQuery(id+"F34.wireOp",EDGE,"E69.sketch_text.stroke-1"),sQuery(id+"F34.wireOp",EDGE,"E69.sketch_text.stroke-2"),sQuery(id+"F34.wireOp",EDGE,"E69.sketch_text.stroke-3"),sQuery(id+"F34.wireOp",EDGE,"E69.sketch_text.stroke-4"),sQuery(id+"F34.wireOp",EDGE,"E69.sketch_text.stroke-5"),sQuery(id+"F34.wireOp",EDGE,"E69.sketch_text.stroke-6"),sQuery(id+"F34.wireOp",EDGE,"E69.sketch_text.stroke-7")])]});
            deleteBodies(context, id + "F40", {"entities" : qUnion([Q0, Q1, Q2, Q3, Q4, Q5, Q6])});
        }
        {
            var Q0;
            Q0=qCreatedBy(makeId("Front.planeOp"),FACE);
            var sketch = newSketch(context, id + "F41", { "sketchPlane" : qUnion([Q0])});
            skText(sketch, "E77", { "text": "RTD", "fontName": "OpenSans-Regular.ttf"});
            const initialGuessF41  = {"E77": [0.11909, 0.005, 1, 0, 0.008]};
            skSetInitialGuess(sketch, initialGuessF41);
            skSolve(sketch);
        }
        {
            var Q0;
            Q0 = qSketchRegion(id + "F41", true);
            extrude(context, id + "F42", {"entities" : qUnion([Q0]), "depth" : 0.5 * mm, "offsetDistance" : 25 * mm});
        }
        {
            var Q0;
            Q0=qCreatedBy(makeId("Front.planeOp"),FACE);
            var sketch = newSketch(context, id + "F43", { "sketchPlane" : qUnion([Q0])});
            skArc(sketch, "E78", {"start": v(96.73, -39.21) * mm, "mid": v(93.71, -36.44) * mm, "end": v(90.93, -33.44) * mm});
            skLineSegment(sketch, "E79", {"start": v(99.5, -30.11) * mm, "end": v(92.6, -32.8) * mm});
            skLineSegment(sketch, "E80", {"start": v(99.5, -30.11) * mm, "end": v(97.26, -37.45) * mm});
            skArc(sketch, "E81", {"start": v(99.54, -39.32) * mm, "mid": v(98.39, -38.4) * mm, "end": v(97.26, -37.45) * mm});
            skArc(sketch, "E82", {"start": v(96.73, -39.21) * mm, "mid": v(97.6, -39.95) * mm, "end": v(98.5, -40.66) * mm});
            skArc(sketch, "E83", {"start": v(90.93, -33.44) * mm, "mid": v(90.14, -32.5) * mm, "end": v(89.38, -31.54) * mm});
            skLineSegment(sketch, "E84", {"start": v(90.71, -30.5) * mm, "end": v(89.38, -31.54) * mm});
            skLineSegment(sketch, "E85", {"start": v(99.54, -39.32) * mm, "end": v(98.5, -40.66) * mm});
            skArc(sketch, "E86.trimOffspring", {"start": v(92.6, -32.8) * mm, "mid": v(91.64, -31.66) * mm, "end": v(90.71, -30.5) * mm});
            skSolve(sketch);
        }
        {
            var Q0;
            Q0 = qSketchRegion(id + "F43", true);
            extrude(context, id + "F44", {"entities" : qUnion([Q0]), "depth" : 0.5 * mm, "offsetDistance" : 25 * mm});
        }
    });
